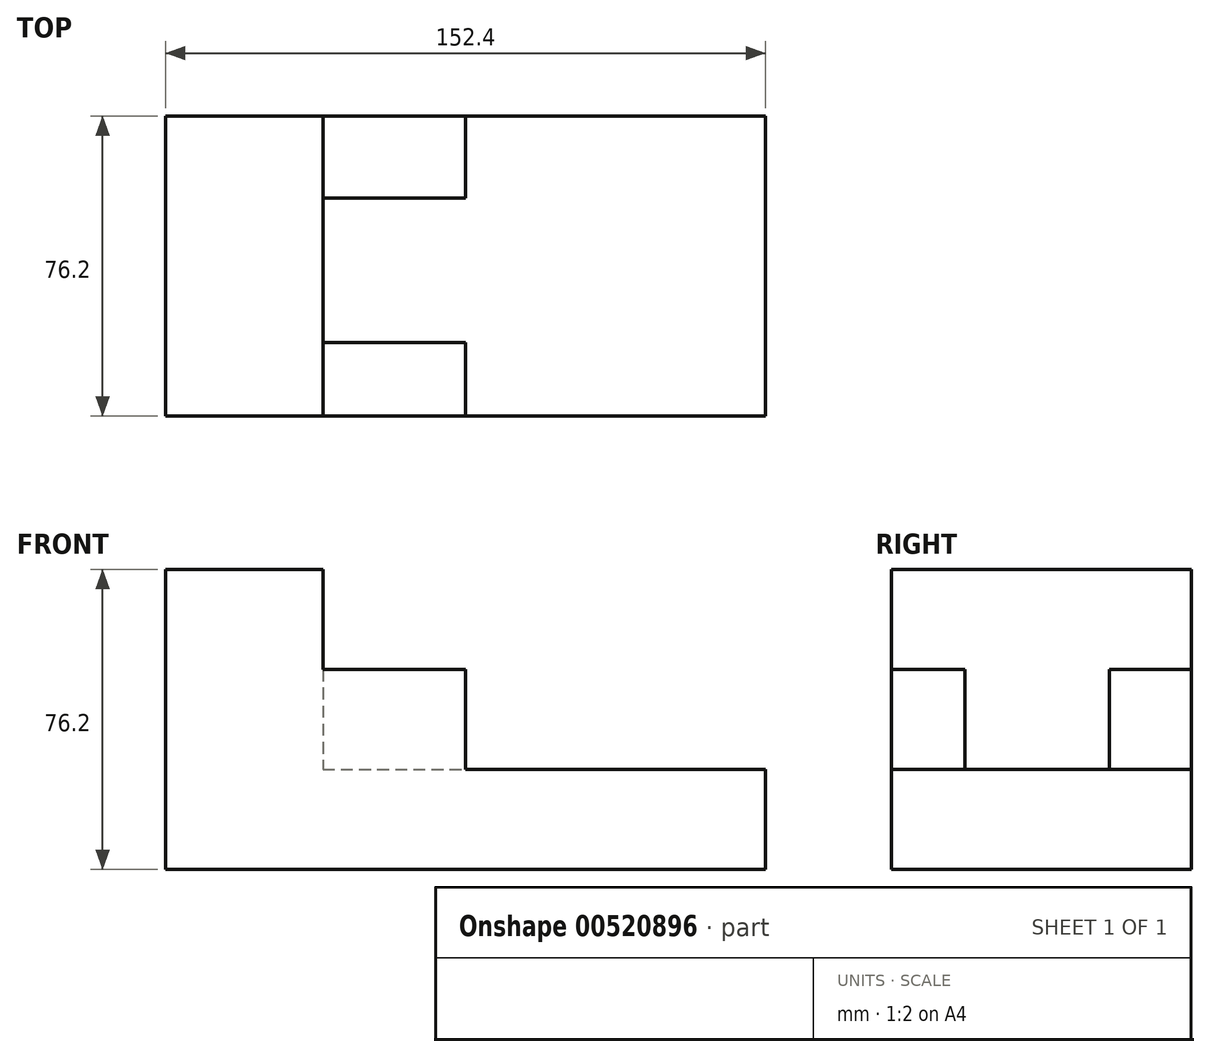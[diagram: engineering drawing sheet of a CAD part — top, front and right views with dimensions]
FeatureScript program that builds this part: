
annotation { "Feature Type Name" : "Feature", "Feature Type Description" : "" }
export const myFeature = defineFeature(function(context is Context, id is Id, definition is map)
    precondition{}
    {
        {
            var Q0;
            Q0=qCreatedBy(makeId("Top.planeOp"),FACE);
            var sketch = newSketch(context, id + "F0", { "sketchPlane" : qUnion([Q0])});
            skLineSegment(sketch, "E0.bottom", {"start": v(-76.2, 38.1) * mm, "end": v(76.2, 38.1) * mm});
            skLineSegment(sketch, "E0.top", {"start": v(-76.2, -38.1) * mm, "end": v(76.2, -38.1) * mm});
            skLineSegment(sketch, "E0.left", {"start": v(-76.2, 38.1) * mm, "end": v(-76.2, -38.1) * mm});
            skLineSegment(sketch, "E0.right", {"start": v(76.2, 38.1) * mm, "end": v(76.2, -38.1) * mm});
            skPoint(sketch, "E0.middle", {"position": v(0, 0) * mm});
            skSolve(sketch);
        }
        {
            var Q0;
            Q0=makeQuery(id+"F0.imprint","IMPRINT",FACE,{"disambiguationData":[TD([[makeQuery(id+"F0.imprint","IMPRINT",EDGE,{"derivedFrom":sQuery(id+"F0.wireOp",EDGE,"E0.bottom")}),-1.0]])]});
            extrude(context, id + "F1", {"entities" : qUnion([Q0]), "depth" : 25.4 * mm, "offsetDistance" : 25.4 * mm});
        }
        {
            var Q0;
            Q0=makeQuery(id+"F1.opExtrude","CAP_FACE",FACE,{"disambiguationData":[OSD([sQuery(id+"F0.wireOp",EDGE,"E0.bottom"),sQuery(id+"F0.wireOp",EDGE,"E0.top"),sQuery(id+"F0.wireOp",EDGE,"E0.left"),sQuery(id+"F0.wireOp",EDGE,"E0.right")])],"isStart":false});
            var sketch = newSketch(context, id + "F2", { "sketchPlane" : qUnion([Q0])});
            skLineSegment(sketch, "E1.bottom", {"start": v(-76.2, 38.1) * mm, "end": v(-36.25, 38.1) * mm});
            skLineSegment(sketch, "E1.top", {"start": v(-76.2, -38.1) * mm, "end": v(-36.25, -38.1) * mm});
            skLineSegment(sketch, "E1.left", {"start": v(-76.2, 38.1) * mm, "end": v(-76.2, -38.1) * mm});
            skLineSegment(sketch, "E1.right", {"start": v(-36.25, 38.1) * mm, "end": v(-36.25, -38.1) * mm});
            skSolve(sketch);
        }
        {
            var Q0;
            Q0=makeQuery(id+"F2.imprint","IMPRINT",FACE,{"disambiguationData":[TD([[makeQuery(id+"F2.imprint","IMPRINT",EDGE,{"derivedFrom":sQuery(id+"F2.wireOp",EDGE,"E1.bottom")}),-1.0]])]});
            extrude(context, id + "F3", {"entities" : qUnion([Q0]), "operationType" : NewBodyOperationType.ADD, "depth" : 50.8 * mm, "offsetDistance" : 25.4 * mm});
        }
        {
            var Q0;
            Q0=makeQuery(id+"F1.opExtrude","CAP_FACE",FACE,{"disambiguationData":[OSD([sQuery(id+"F0.wireOp",EDGE,"E0.bottom"),sQuery(id+"F0.wireOp",EDGE,"E0.top"),sQuery(id+"F0.wireOp",EDGE,"E0.left"),sQuery(id+"F0.wireOp",EDGE,"E0.right")])],"isStart":false});
            var sketch = newSketch(context, id + "F4", { "sketchPlane" : qUnion([Q0])});
            skLineSegment(sketch, "E2.bottom", {"start": v(-36.25, 38.1) * mm, "end": v(0, 38.1) * mm});
            skLineSegment(sketch, "E2.top", {"start": v(-36.25, 17.26) * mm, "end": v(0, 17.26) * mm});
            skLineSegment(sketch, "E2.left", {"start": v(-36.25, 38.1) * mm, "end": v(-36.25, 17.26) * mm});
            skLineSegment(sketch, "E2.right", {"start": v(0, 38.1) * mm, "end": v(0, 17.26) * mm});
            skLineSegment(sketch, "E3.bottom", {"start": v(-36.25, -38.1) * mm, "end": v(0, -38.1) * mm});
            skLineSegment(sketch, "E3.top", {"start": v(-36.25, -19.47) * mm, "end": v(0, -19.47) * mm});
            skLineSegment(sketch, "E3.left", {"start": v(-36.25, -38.1) * mm, "end": v(-36.25, -19.47) * mm});
            skLineSegment(sketch, "E3.right", {"start": v(0, -38.1) * mm, "end": v(0, -19.47) * mm});
            skSolve(sketch);
        }
        {
            var Q0;
            Q0=makeQuery(id+"F4.imprint","IMPRINT",FACE,{"disambiguationData":[TD([[makeQuery(id+"F4.imprint","IMPRINT",EDGE,{"derivedFrom":sQuery(id+"F4.wireOp",EDGE,"E2.bottom")}),-1.0]])]});
            var Q1;
            Q1=makeQuery(id+"F4.imprint","IMPRINT",FACE,{"disambiguationData":[TD([[makeQuery(id+"F4.imprint","IMPRINT",EDGE,{"derivedFrom":sQuery(id+"F4.wireOp",EDGE,"E3.bottom")}),1.0]])]});
            var Q2;
            Q2=sQuery(id+"F4.wireOp",EDGE,"E2.top");
            extrude(context, id + "F5", {"entities" : qUnion([Q0, Q1]), "operationType" : NewBodyOperationType.ADD, "surfaceEntities" : qUnion([Q2]), "depth" : 25.4 * mm, "offsetDistance" : 25.4 * mm});
        }
    });
